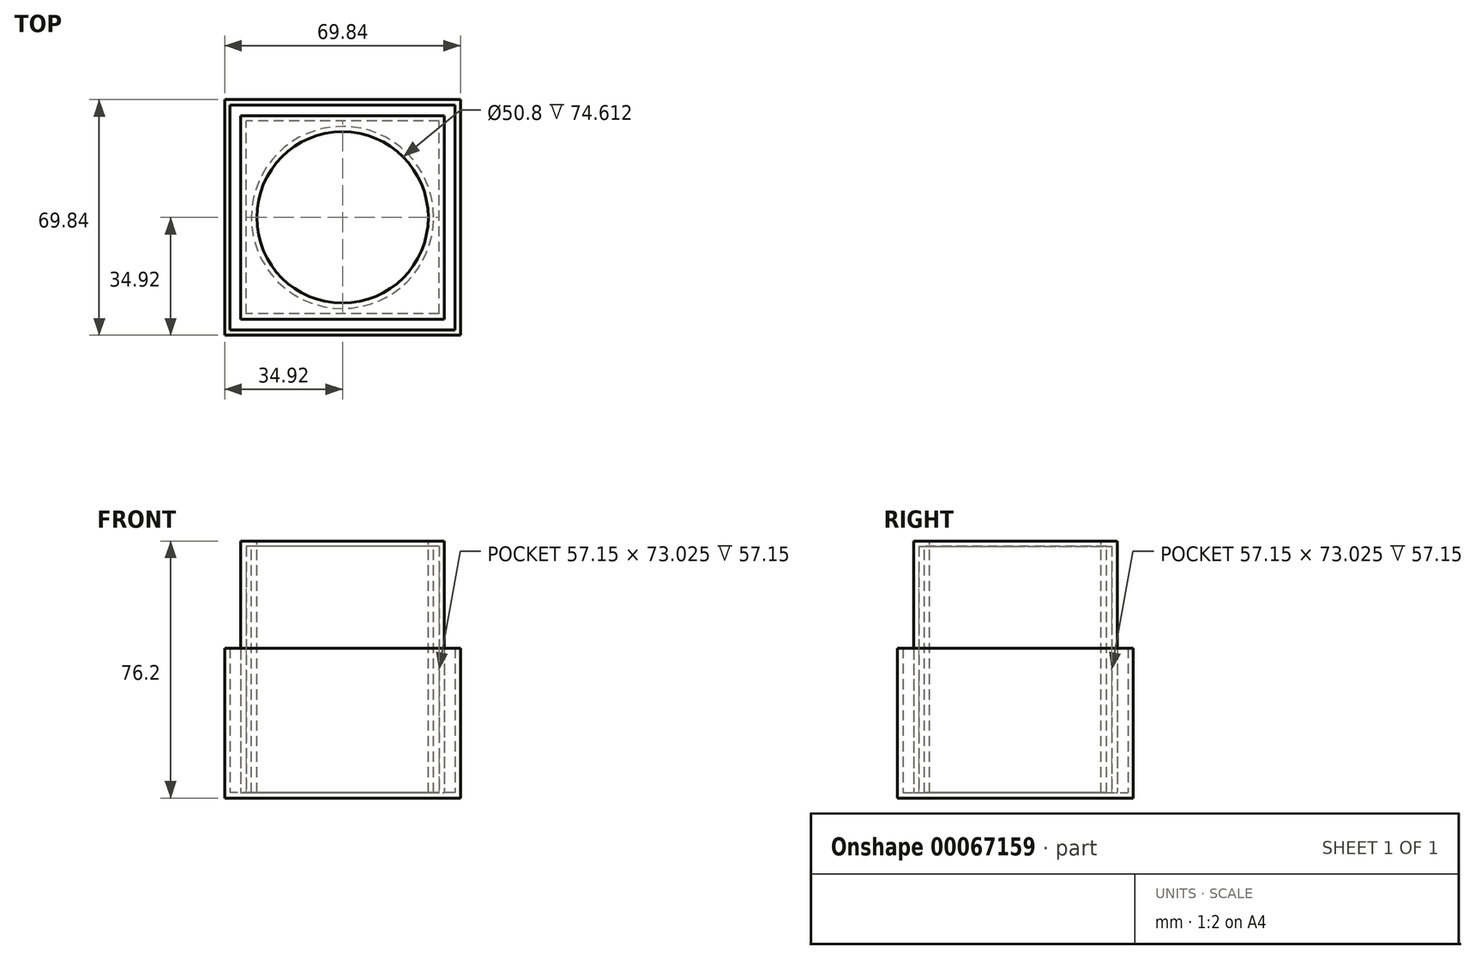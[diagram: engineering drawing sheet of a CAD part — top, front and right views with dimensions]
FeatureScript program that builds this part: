
annotation { "Feature Type Name" : "Feature", "Feature Type Description" : "" }
export const myFeature = defineFeature(function(context is Context, id is Id, definition is map)
    precondition{}
    {
        {
            var Q0;
            Q0=qCreatedBy(makeId("Top.planeOp"),FACE);
            var sketch = newSketch(context, id + "F0", { "sketchPlane" : qUnion([Q0])});
            skLineSegment(sketch, "E0.bottom", {"start": v(-34.92, 34.92) * mm, "end": v(34.92, 34.93) * mm});
            skLineSegment(sketch, "E0.top", {"start": v(-34.92, -34.93) * mm, "end": v(34.92, -34.92) * mm});
            skLineSegment(sketch, "E0.left", {"start": v(-34.93, 34.93) * mm, "end": v(-34.92, -34.93) * mm});
            skLineSegment(sketch, "E0.right", {"start": v(34.92, 34.93) * mm, "end": v(34.93, -34.93) * mm});
            skSolve(sketch);
        }
        {
            var Q0;
            Q0=makeQuery(id+"F0.imprint","IMPRINT",FACE,{"disambiguationData":[TD([[makeQuery(id+"F0.imprint","IMPRINT",EDGE,{"derivedFrom":sQuery(id+"F0.wireOp",EDGE,"E0.bottom")}),-1.0]])]});
            extrude(context, id + "F1", {"entities" : qUnion([Q0]), "depth" : 1.59 * mm});
        }
        {
            var Q0;
            Q0=makeQuery(id+"F1.opExtrude","CAP_FACE",FACE,{"disambiguationData":[OSD([sQuery(id+"F0.wireOp",EDGE,"E0.bottom"),sQuery(id+"F0.wireOp",EDGE,"E0.top"),sQuery(id+"F0.wireOp",EDGE,"E0.left"),sQuery(id+"F0.wireOp",EDGE,"E0.right")])],"isStart":false});
            var sketch = newSketch(context, id + "F2", { "sketchPlane" : qUnion([Q0])});
            skLineSegment(sketch, "E1.bottom", {"start": v(33.34, -33.34) * mm, "end": v(-33.34, -33.34) * mm});
            skLineSegment(sketch, "E1.top", {"start": v(33.34, 33.34) * mm, "end": v(-33.34, 33.34) * mm});
            skLineSegment(sketch, "E1.left", {"start": v(33.34, -33.34) * mm, "end": v(33.34, 33.34) * mm});
            skLineSegment(sketch, "E1.right", {"start": v(-33.34, -33.34) * mm, "end": v(-33.34, 33.34) * mm});
            skSolve(sketch);
        }
        {
            var Q0;
            Q0=makeQuery(id+"F2.imprint","IMPRINT",FACE,{"disambiguationData":[TD([[makeQuery(id+"F2.imprint","IMPRINT",EDGE,{"derivedFrom":sQuery(id+"F2.wireOp",EDGE,"E1.bottom")}),1.0]])]});
            extrude(context, id + "F3", {"entities" : qUnion([Q0]), "operationType" : NewBodyOperationType.ADD, "depth" : 42.86 * mm});
        }
        {
            var Q0;
            Q0=makeQuery(id+"F1.opExtrude","CAP_FACE",FACE,{"disambiguationData":[OSD([sQuery(id+"F0.wireOp",EDGE,"E0.bottom"),sQuery(id+"F0.wireOp",EDGE,"E0.top"),sQuery(id+"F0.wireOp",EDGE,"E0.left"),sQuery(id+"F0.wireOp",EDGE,"E0.right")])],"isStart":false});
            var sketch = newSketch(context, id + "F4", { "sketchPlane" : qUnion([Q0])});
            skLineSegment(sketch, "E2.bottom", {"start": v(-30.16, -30.16) * mm, "end": v(30.16, -30.16) * mm});
            skLineSegment(sketch, "E2.top", {"start": v(-30.16, 30.16) * mm, "end": v(30.16, 30.16) * mm});
            skLineSegment(sketch, "E2.left", {"start": v(-30.16, -30.16) * mm, "end": v(-30.16, 30.16) * mm});
            skLineSegment(sketch, "E2.right", {"start": v(30.16, -30.16) * mm, "end": v(30.16, 30.16) * mm});
            skLineSegment(sketch, "E3.bottom", {"start": v(-28.58, -28.58) * mm, "end": v(28.58, -28.58) * mm});
            skLineSegment(sketch, "E3.top", {"start": v(-28.58, 28.58) * mm, "end": v(28.58, 28.58) * mm});
            skLineSegment(sketch, "E3.left", {"start": v(-28.57, -28.58) * mm, "end": v(-28.58, 28.58) * mm});
            skLineSegment(sketch, "E3.right", {"start": v(28.58, -28.58) * mm, "end": v(28.57, 28.58) * mm});
            skSolve(sketch);
        }
        {
            var Q0;
            Q0=makeQuery(id+"F4.imprint","IMPRINT",FACE,{"disambiguationData":[TD([[makeQuery(id+"F4.imprint","IMPRINT",EDGE,{"derivedFrom":sQuery(id+"F4.wireOp",EDGE,"E2.bottom")}),1.0]])]});
            extrude(context, id + "F5", {"entities" : qUnion([Q0]), "operationType" : NewBodyOperationType.ADD, "depth" : 74.61 * mm});
        }
        {
            var Q0;
            Q0=makeQuery(id+"F5.opExtrude","SWEPT_FACE",FACE,{"disambiguationData":[OSD([sQuery(id+"F4.wireOp",EDGE,"E3.left")])]});
            var sketch = newSketch(context, id + "F6", { "sketchPlane" : qUnion([Q0])});
            skLineSegment(sketch, "E4.bottom", {"start": v(-28.58, 76.2) * mm, "end": v(28.58, 76.2) * mm});
            skLineSegment(sketch, "E4.top", {"start": v(-28.58, 74.61) * mm, "end": v(28.58, 74.61) * mm});
            skLineSegment(sketch, "E4.left", {"start": v(-28.58, 76.2) * mm, "end": v(-28.58, 74.61) * mm});
            skLineSegment(sketch, "E4.right", {"start": v(28.58, 76.2) * mm, "end": v(28.58, 74.61) * mm});
            skSolve(sketch);
        }
        {
            var Q0;
            Q0=makeQuery(id+"F6.imprint","IMPRINT",FACE,{"disambiguationData":[TD([[makeQuery(id+"F6.imprint","IMPRINT",EDGE,{"derivedFrom":sQuery(id+"F6.wireOp",EDGE,"E4.bottom")}),-1.0]])]});
            extrude(context, id + "F7", {"entities" : qUnion([Q0]), "operationType" : NewBodyOperationType.ADD, "depth" : 58.74 * mm});
        }
        {
            var Q0;
            Q0=makeQuery(id+"F7.boolean.opBoolean","MERGE",FACE,{"derivedFrom":[makeQuery(id+"F5.opExtrude","CAP_FACE",FACE,{"disambiguationData":[OSD([sQuery(id+"F4.wireOp",EDGE,"E2.bottom"),sQuery(id+"F4.wireOp",EDGE,"E2.top"),sQuery(id+"F4.wireOp",EDGE,"E2.left"),sQuery(id+"F4.wireOp",EDGE,"E2.right"),sQuery(id+"F4.wireOp",EDGE,"E3.bottom"),sQuery(id+"F4.wireOp",EDGE,"E3.top"),sQuery(id+"F4.wireOp",EDGE,"E3.left"),sQuery(id+"F4.wireOp",EDGE,"E3.right")])],"isStart":false}),makeQuery(id+"F7.opExtrude","SWEPT_FACE",FACE,{"disambiguationData":[OSD([sQuery(id+"F6.wireOp",EDGE,"E4.bottom")])]})]});
            var sketch = newSketch(context, id + "F8", { "sketchPlane" : qUnion([Q0])});
            skCircle(sketch, "E5", {"center": v(0, 0) * mm, "radius": 25.4 * mm});
            skSolve(sketch);
        }
        {
            var Q0;
            Q0 = qSketchRegion(id + "F8", true);
            extrude(context, id + "F9", {"entities" : qUnion([Q0]), "operationType" : NewBodyOperationType.REMOVE, "oppositeDirection" : true, "depth" : 74.61 * mm});
        }
        {
            var Q0;
            Q0=makeQuery(id+"F7.boolean.opBoolean","MERGE",FACE,{"derivedFrom":[makeQuery(id+"F5.opExtrude","CAP_FACE",FACE,{"disambiguationData":[OSD([sQuery(id+"F4.wireOp",EDGE,"E2.bottom"),sQuery(id+"F4.wireOp",EDGE,"E2.top"),sQuery(id+"F4.wireOp",EDGE,"E2.left"),sQuery(id+"F4.wireOp",EDGE,"E2.right"),sQuery(id+"F4.wireOp",EDGE,"E3.bottom"),sQuery(id+"F4.wireOp",EDGE,"E3.top"),sQuery(id+"F4.wireOp",EDGE,"E3.left"),sQuery(id+"F4.wireOp",EDGE,"E3.right")])],"isStart":false}),makeQuery(id+"F7.opExtrude","SWEPT_FACE",FACE,{"disambiguationData":[OSD([sQuery(id+"F6.wireOp",EDGE,"E4.bottom")])]})]});
            var sketch = newSketch(context, id + "F10", { "sketchPlane" : qUnion([Q0])});
            skCircle(sketch, "E6", {"center": v(0, 0) * mm, "radius": 26.99 * mm});
            skSolve(sketch);
        }
        {
            var Q0;
            Q0=makeQuery(id+"F10.imprint","IMPRINT",FACE,{"disambiguationData":[TD([[makeQuery(id+"F10.imprint","IMPRINT",EDGE,{"derivedFrom":sQuery(id+"F10.wireOp",EDGE,"E6")}),1.0]])]});
            extrude(context, id + "F11", {"entities" : qUnion([Q0]), "operationType" : NewBodyOperationType.ADD, "oppositeDirection" : true, "depth" : 76.2 * mm});
        }
    });
